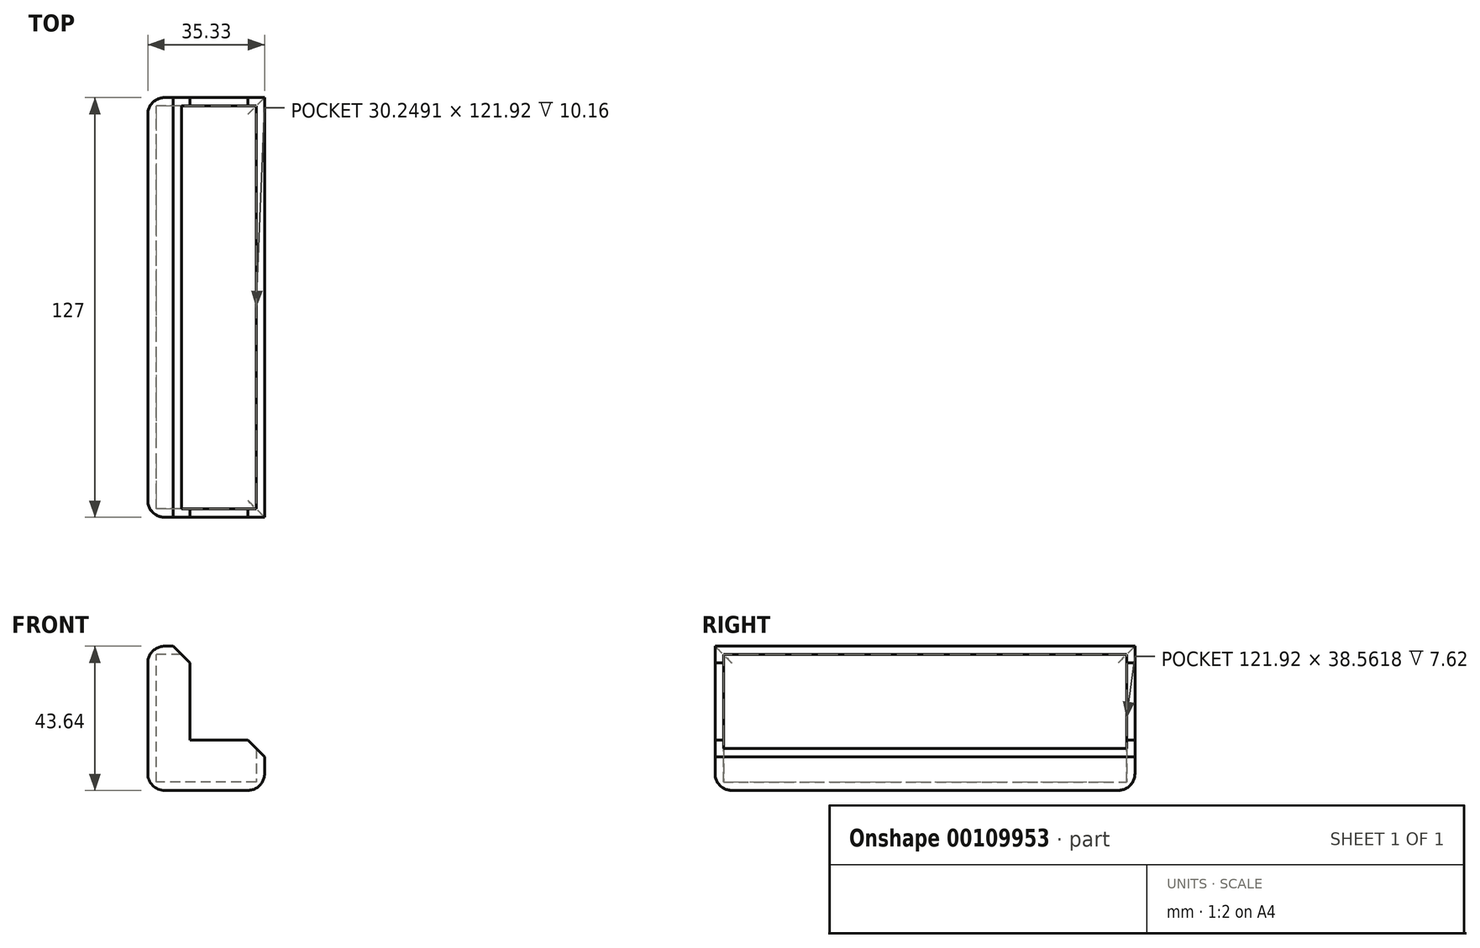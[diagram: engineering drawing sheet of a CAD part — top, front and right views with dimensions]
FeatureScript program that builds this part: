
annotation { "Feature Type Name" : "Feature", "Feature Type Description" : "" }
export const myFeature = defineFeature(function(context is Context, id is Id, definition is map)
    precondition{}
    {
        {
            var Q0;
            Q0=qCreatedBy(makeId("Front.planeOp"),FACE);
            var sketch = newSketch(context, id + "F0", { "sketchPlane" : qUnion([Q0])});
            skLineSegment(sketch, "E0.bottom", {"start": v(-22.63, 15.24) * mm, "end": v(0, 15.24) * mm});
            skLineSegment(sketch, "E0.top", {"start": v(-22.63, 0) * mm, "end": v(0, 0) * mm});
            skLineSegment(sketch, "E0.left", {"start": v(-22.63, 15.24) * mm, "end": v(-22.63, 0) * mm});
            skLineSegment(sketch, "E0.right", {"start": v(0, 15.24) * mm, "end": v(0, 0) * mm});
            skLineSegment(sketch, "E1.bottom", {"start": v(-22.63, 0) * mm, "end": v(-35.33, 0) * mm});
            skLineSegment(sketch, "E1.top", {"start": v(-22.63, 43.64) * mm, "end": v(-35.33, 43.64) * mm});
            skLineSegment(sketch, "E1.left", {"start": v(-22.63, 0) * mm, "end": v(-22.63, 43.64) * mm});
            skLineSegment(sketch, "E1.right", {"start": v(-35.33, 0) * mm, "end": v(-35.33, 43.64) * mm});
            skSolve(sketch);
        }
        {
            var Q0;
            {var subQ3=sQuery(id+"F0.wireOp",EDGE,"E1.bottom");Q0=makeQuery(id+"F0.imprint","IMPRINT",FACE,{"disambiguationData":[TD([[makeQuery(id+"F0.imprint","IMPRINT",EDGE,{"derivedFrom":subQ3}),-1.0]])]});}
            var Q1;
            {var subQ0=sQuery(id+"F0.wireOp",EDGE,"E0.bottom");Q1=makeQuery(id+"F0.imprint","IMPRINT",FACE,{"disambiguationData":[TD([[makeQuery(id+"F0.imprint","IMPRINT",EDGE,{"derivedFrom":subQ0}),-1.0]])]});}
            extrude(context, id + "F1", {"entities" : qUnion([Q0, Q1]), "depth" : 127 * mm});
        }
        {
            var Q0;
            Q0=makeQuery(id+"F1.opExtrude","SWEPT_FACE",FACE,{"disambiguationData":[OSD([sQuery(id+"F0.wireOp",EDGE,"E1.left")])]});
            var Q1;
            Q1=makeQuery(id+"F1.opExtrude","SWEPT_FACE",FACE,{"disambiguationData":[OSD([sQuery(id+"F0.wireOp",EDGE,"E0.bottom")])]});
            shell(context, id + "F2", {"entities" : qUnion([Q0, Q1]), "thickness" : 2.54 * mm});
        }
        {
            var Q0;
            Q0=makeQuery(id+"F1.opExtrude","SWEPT_EDGE",EDGE,{"disambiguationData":[OSD([sQuery(id+"F0.wireOp",EDGE,"E1.top"),sQuery(id+"F0.wireOp",EDGE,"E1.right")])]});
            var Q1;
            Q1=makeQuery(id+"F1.opExtrude","SWEPT_EDGE",EDGE,{"disambiguationData":[OSD([sQuery(id+"F0.wireOp",EDGE,"E0.top"),sQuery(id+"F0.wireOp",EDGE,"E0.right")])]});
            var Q2;
            Q2=makeQuery(id+"F1.opExtrude","SWEPT_FACE",FACE,{"disambiguationData":[OSD([sQuery(id+"F0.wireOp",EDGE,"E1.right")])]});
            var Q3;
            Q3=makeQuery(id+"F1.opExtrude","CAP_EDGE",EDGE,{"disambiguationData":[OSD([sQuery(id+"F0.wireOp",EDGE,"E0.top"),sQuery(id+"F0.wireOp",EDGE,"E1.bottom")])],"isStart":false});
            var Q4;
            Q4=makeQuery(id+"F1.opExtrude","CAP_EDGE",EDGE,{"disambiguationData":[OSD([sQuery(id+"F0.wireOp",EDGE,"E0.top"),sQuery(id+"F0.wireOp",EDGE,"E1.bottom")])],"isStart":true});
            fillet(context, id + "F3", {"entities" : qUnion([Q0, Q1, Q2, Q3, Q4]), "radius" : 5.08 * mm, "tangentPropagation" : true, "allowEdgeOverflow" : false});
        }
        {
            var Q0;
            Q0=makeQuery(id+"F1.opExtrude","SWEPT_EDGE",EDGE,{"disambiguationData":[OSD([sQuery(id+"F0.wireOp",EDGE,"E1.top"),sQuery(id+"F0.wireOp",EDGE,"E1.left")])]});
            var Q1;
            Q1=makeQuery(id+"F1.opExtrude","SWEPT_EDGE",EDGE,{"disambiguationData":[OSD([sQuery(id+"F0.wireOp",EDGE,"E0.bottom"),sQuery(id+"F0.wireOp",EDGE,"E0.right")])]});
            chamfer(context, id + "F4", {"entities" : qUnion([Q0, Q1]), "width" : 5.08 * mm, "tangentPropagation" : true});
        }
    });
